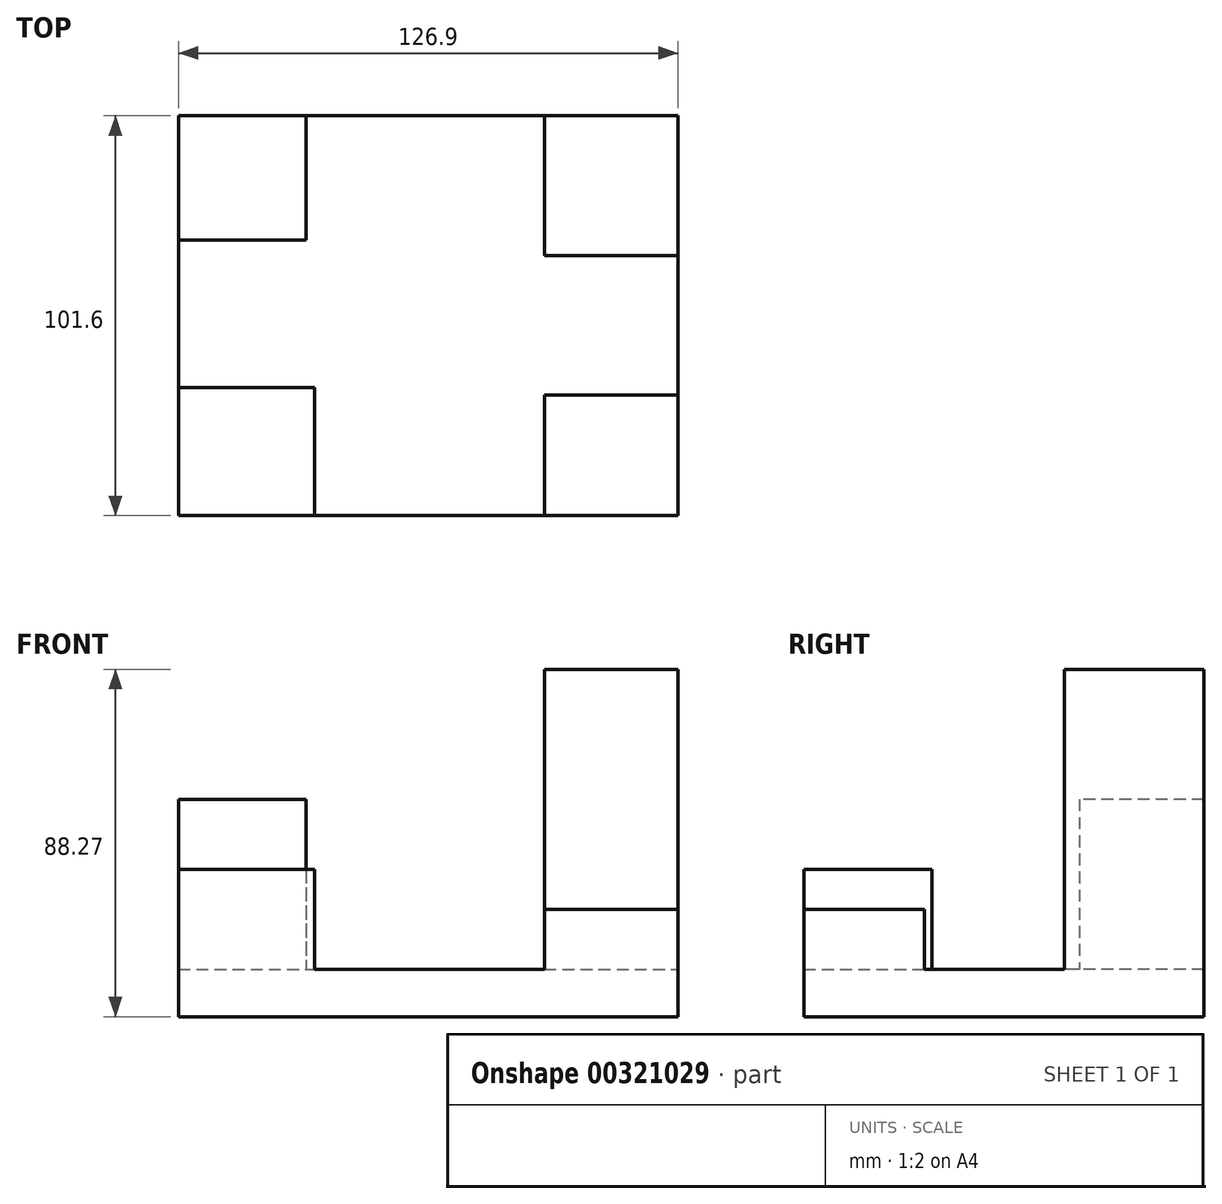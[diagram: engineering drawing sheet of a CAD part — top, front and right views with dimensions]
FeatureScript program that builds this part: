
annotation { "Feature Type Name" : "Feature", "Feature Type Description" : "" }
export const myFeature = defineFeature(function(context is Context, id is Id, definition is map)
    precondition{}
    {
        {
            var Q0;
            Q0=qCreatedBy(makeId("Front.planeOp"),FACE);
            var sketch = newSketch(context, id + "F0", { "sketchPlane" : qUnion([Q0])});
            skLineSegment(sketch, "E0.bottom", {"start": v(-62.83, -46.27) * mm, "end": v(64.07, -46.27) * mm});
            skLineSegment(sketch, "E0.top", {"start": v(-62.83, -58.34) * mm, "end": v(64.07, -58.34) * mm});
            skLineSegment(sketch, "E0.left", {"start": v(-62.83, -46.27) * mm, "end": v(-62.83, -58.34) * mm});
            skLineSegment(sketch, "E0.right", {"start": v(64.07, -46.27) * mm, "end": v(64.07, -58.34) * mm});
            skSolve(sketch);
        }
        {
            var Q0;
            Q0=makeQuery(id+"F0.imprint","IMPRINT",FACE,{"disambiguationData":[TD([[makeQuery(id+"F0.imprint","IMPRINT",EDGE,{"derivedFrom":sQuery(id+"F0.wireOp",EDGE,"E0.bottom")}),-1.0]])]});
            extrude(context, id + "F1", {"entities" : qUnion([Q0]), "oppositeDirection" : true, "depth" : 101.6 * mm});
        }
        {
            var Q0;
            Q0=makeQuery(id+"F1.opExtrude","SWEPT_FACE",FACE,{"disambiguationData":[OSD([sQuery(id+"F0.wireOp",EDGE,"E0.bottom")])]});
            var sketch = newSketch(context, id + "F2", { "sketchPlane" : qUnion([Q0])});
            skLineSegment(sketch, "E1.bottom", {"start": v(30.15, 0) * mm, "end": v(64.07, 0) * mm});
            skLineSegment(sketch, "E1.top", {"start": v(30.15, 30.68) * mm, "end": v(64.07, 30.68) * mm});
            skLineSegment(sketch, "E1.left", {"start": v(30.15, 0) * mm, "end": v(30.15, 30.68) * mm});
            skLineSegment(sketch, "E1.right", {"start": v(64.07, 0) * mm, "end": v(64.07, 30.68) * mm});
            skSolve(sketch);
        }
        {
            var Q0;
            Q0=makeQuery(id+"F2.imprint","IMPRINT",FACE,{"disambiguationData":[TD([[makeQuery(id+"F2.imprint","IMPRINT",EDGE,{"derivedFrom":sQuery(id+"F2.wireOp",EDGE,"E1.bottom")}),1.0]])]});
            extrude(context, id + "F3", {"entities" : qUnion([Q0]), "operationType" : NewBodyOperationType.ADD, "depth" : 15.24 * mm});
        }
        {
            var Q0;
            Q0=makeQuery(id+"F1.opExtrude","SWEPT_FACE",FACE,{"disambiguationData":[OSD([sQuery(id+"F0.wireOp",EDGE,"E0.bottom")])]});
            var sketch = newSketch(context, id + "F4", { "sketchPlane" : qUnion([Q0])});
            skLineSegment(sketch, "E2.bottom", {"start": v(-62.83, 0) * mm, "end": v(-28.2, 0) * mm});
            skLineSegment(sketch, "E2.top", {"start": v(-62.83, 32.53) * mm, "end": v(-28.2, 32.53) * mm});
            skLineSegment(sketch, "E2.left", {"start": v(-62.83, 0) * mm, "end": v(-62.83, 32.53) * mm});
            skLineSegment(sketch, "E2.right", {"start": v(-28.2, 0) * mm, "end": v(-28.2, 32.53) * mm});
            skSolve(sketch);
        }
        {
            var Q0;
            Q0=makeQuery(id+"F4.imprint","IMPRINT",FACE,{"disambiguationData":[TD([[makeQuery(id+"F4.imprint","IMPRINT",EDGE,{"derivedFrom":sQuery(id+"F4.wireOp",EDGE,"E2.bottom")}),1.0]])]});
            extrude(context, id + "F5", {"entities" : qUnion([Q0]), "operationType" : NewBodyOperationType.ADD, "depth" : 25.4 * mm});
        }
        {
            var Q0;
            Q0=makeQuery(id+"F1.opExtrude","SWEPT_FACE",FACE,{"disambiguationData":[OSD([sQuery(id+"F0.wireOp",EDGE,"E0.bottom")])]});
            var sketch = newSketch(context, id + "F6", { "sketchPlane" : qUnion([Q0])});
            skLineSegment(sketch, "E3.bottom", {"start": v(-62.83, 101.6) * mm, "end": v(-30.44, 101.6) * mm});
            skLineSegment(sketch, "E3.top", {"start": v(-62.83, 69.99) * mm, "end": v(-30.44, 69.99) * mm});
            skLineSegment(sketch, "E3.left", {"start": v(-62.83, 101.6) * mm, "end": v(-62.83, 69.99) * mm});
            skLineSegment(sketch, "E3.right", {"start": v(-30.44, 101.6) * mm, "end": v(-30.44, 69.99) * mm});
            skSolve(sketch);
        }
        {
            var Q0;
            Q0=makeQuery(id+"F6.imprint","IMPRINT",FACE,{"disambiguationData":[TD([[makeQuery(id+"F6.imprint","IMPRINT",EDGE,{"derivedFrom":sQuery(id+"F6.wireOp",EDGE,"E3.bottom")}),-1.0]])]});
            extrude(context, id + "F7", {"entities" : qUnion([Q0]), "operationType" : NewBodyOperationType.ADD, "depth" : 43.18 * mm});
        }
        {
            var Q0;
            Q0=makeQuery(id+"F1.opExtrude","SWEPT_FACE",FACE,{"disambiguationData":[OSD([sQuery(id+"F0.wireOp",EDGE,"E0.bottom")])]});
            var sketch = newSketch(context, id + "F8", { "sketchPlane" : qUnion([Q0])});
            skPoint(sketch, "E4.firstSnap0", {"position": v(30.15, 15.34) * mm});
            skLineSegment(sketch, "E4.bottom", {"start": v(30.15, 101.6) * mm, "end": v(64.07, 101.6) * mm});
            skLineSegment(sketch, "E4.top", {"start": v(30.15, 66.14) * mm, "end": v(64.07, 66.14) * mm});
            skLineSegment(sketch, "E4.left", {"start": v(30.15, 101.6) * mm, "end": v(30.15, 66.14) * mm});
            skLineSegment(sketch, "E4.right", {"start": v(64.07, 101.6) * mm, "end": v(64.07, 66.14) * mm});
            skSolve(sketch);
        }
        {
            var Q0;
            Q0=makeQuery(id+"F8.imprint","IMPRINT",FACE,{"disambiguationData":[TD([[makeQuery(id+"F8.imprint","IMPRINT",EDGE,{"derivedFrom":sQuery(id+"F8.wireOp",EDGE,"E4.bottom")}),-1.0]])]});
            extrude(context, id + "F9", {"entities" : qUnion([Q0]), "operationType" : NewBodyOperationType.ADD, "depth" : 76.2 * mm});
        }
    });
